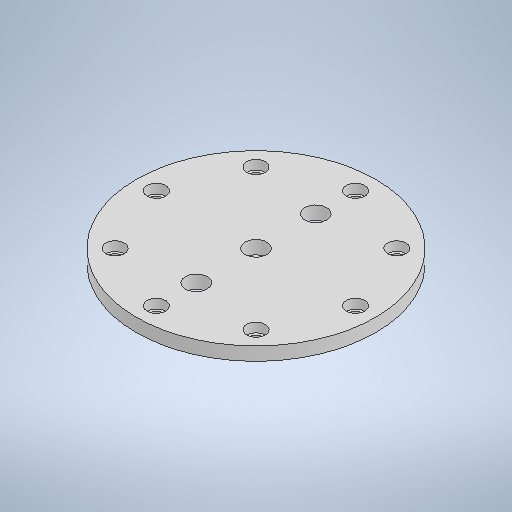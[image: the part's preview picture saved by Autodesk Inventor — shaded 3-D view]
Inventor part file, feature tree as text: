
AUTODESK INVENTOR PART (.ipt)
format: ipt  version: 2025.2 (Build 292293000, 293)  size: 244,736 bytes
history: native  units: mm
features: sketch x3, extrude x2, hole x1, pattern_circular x1
ambient origin geometry x8: Origin, YZ Plane, XZ Plane, XY Plane, X Axis, Y Axis, Z Axis, Center Point
bodies: Solid1 (feature_tree)
feature tree (7):
  extrude  "Extrusion1"  Depth=5.0mm TaperAngle=0.0deg
  sketch  "Sketch2"  dims[d12=8.2mm d14=45.0mm]
  extrude  "Extrusion3"  Depth=45.0mm
  hole  "Hole1"  [1 undecoded]
  pattern_circular  "Circular Pattern2"  Count=8 Angle=360.0deg
  sketch  "Sketch1"  dims[d0=90.0mm d3=5.0mm d4=0.0mm]
  sketch  "Sketch3"  dims[d15=0.0mm d16=0.0mm d17=37.5mm d18=5.0mm d19=6.0mm d20=7.0mm d21=3.5mm d22=90.0deg d23=8.0mm d24=20.594885mm d25=80.0mm d26=360.0deg d5=0.5mm d6=0.872665mm]
note: 1 required parameter value undecoded (feature->parameter linkage not recoverable at this tier; creation-order binding heuristic only, values carry confidence <= 0.55)
